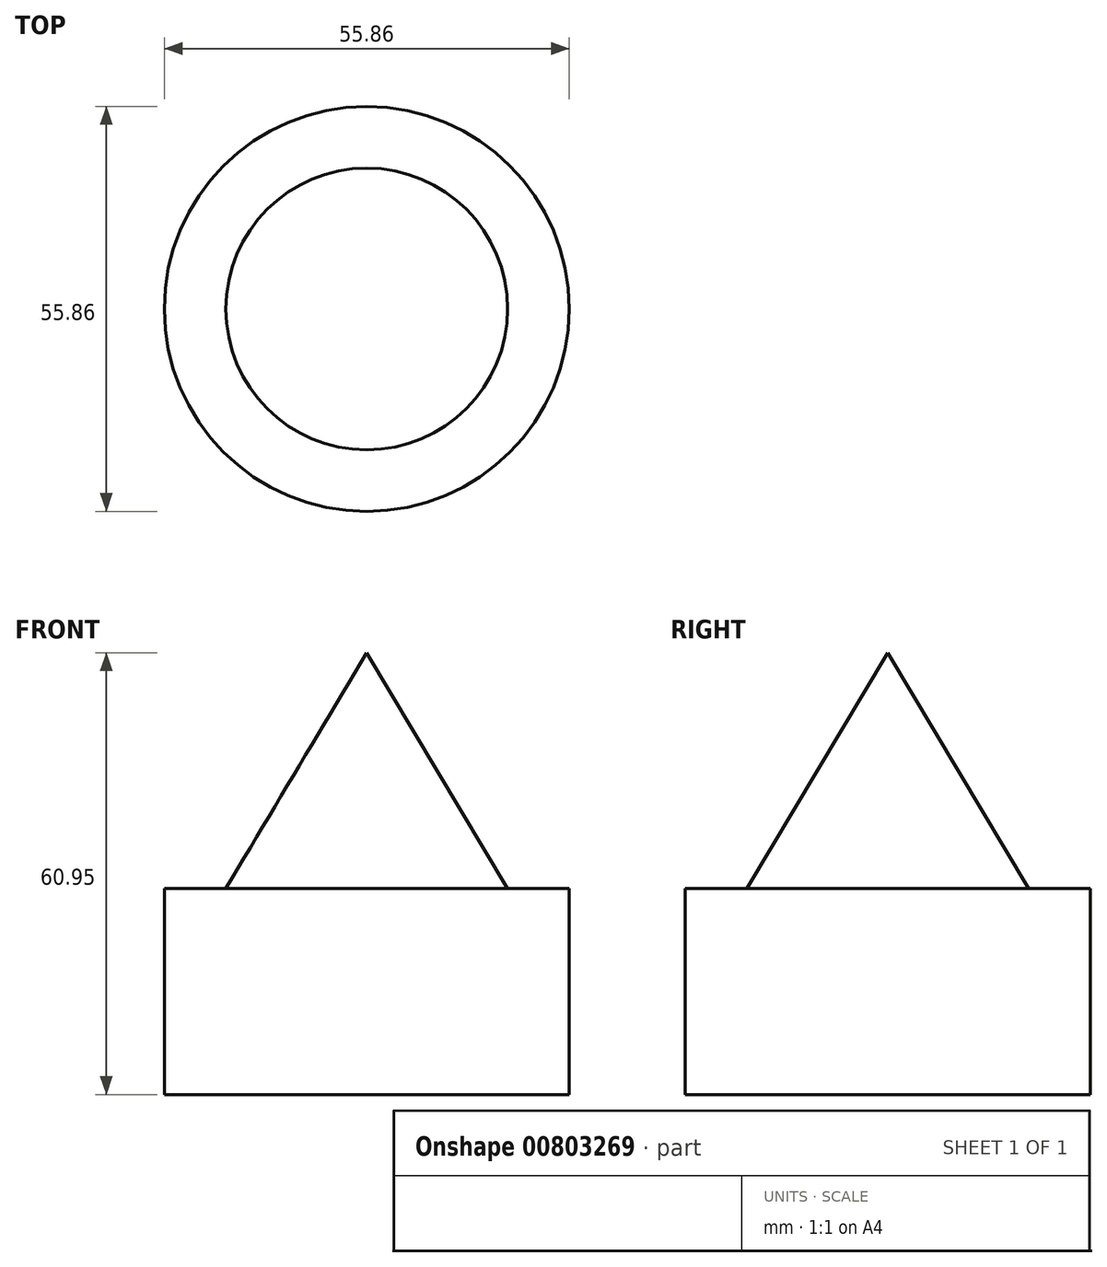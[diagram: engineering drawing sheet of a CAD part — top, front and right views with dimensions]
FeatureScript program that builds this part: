
annotation { "Feature Type Name" : "Feature", "Feature Type Description" : "" }
export const myFeature = defineFeature(function(context is Context, id is Id, definition is map)
    precondition{}
    {
        {
            var Q0;
            Q0=qCreatedBy(makeId("Front.planeOp"),FACE);
            var sketch = newSketch(context, id + "F0", { "sketchPlane" : qUnion([Q0])});
            skLineSegment(sketch, "E0", {"start": v(0, 0) * mm, "end": v(0, 46.73) * mm});
            skLineSegment(sketch, "E1", {"start": v(0, 46.73) * mm, "end": v(27.93, 0) * mm});
            skLineSegment(sketch, "E2", {"start": v(27.93, 0) * mm, "end": v(0, 0) * mm});
            skSolve(sketch);
        }
        {
            var Q0;
            Q0 = qSketchRegion(id + "F0", true);
            var Q1;
            Q1=sQuery(id+"F0.wireOp",EDGE,"E0");
            revolve(context, id + "F1", {"surfaceOperationType" : NewSurfaceOperationType.NEW, "entities" : qUnion([Q0]), "axis" : qUnion([Q1]), "revolveType" : RevolveType.FULL});
        }
        {
            var Q0;
            Q0=qCreatedBy(makeId("Right.planeOp"),FACE);
            var sketch = newSketch(context, id + "F2", { "sketchPlane" : qUnion([Q0])});
            skLineSegment(sketch, "E3", {"start": v(-15.95, 50.24) * mm, "end": v(-15.95, -22.77) * mm});
            skSolve(sketch);
        }
        {
            var Q0;
            Q0=sQuery(id+"F2.wireOp",EDGE,"E3");
            extrude(context, id + "F3", {"bodyType" : ToolBodyType.SURFACE, "surfaceEntities" : qUnion([Q0]), "endBound" : BoundingType.SYMMETRIC, "depth" : 80.26 * mm, "offsetDistance" : 25.4 * mm});
        }
        {
            var Q0;
            Q0=qCreatedBy(makeId("Right.planeOp"),FACE);
            var sketch = newSketch(context, id + "F4", { "sketchPlane" : qUnion([Q0])});
            skLineSegment(sketch, "E4", {"start": v(-36.04, 26.27) * mm, "end": v(37.52, 26.27) * mm});
            skSolve(sketch);
        }
        {
            var Q0;
            Q0 = qSketchRegion(id + "F4", true);
            var Q1;
            Q1=sQuery(id+"F4.wireOp",EDGE,"E4");
            extrude(context, id + "F5", {"entities" : qUnion([Q0]), "bodyType" : ToolBodyType.SURFACE, "surfaceEntities" : qUnion([Q1]), "endBound" : BoundingType.SYMMETRIC, "depth" : 92.96 * mm, "offsetDistance" : 25.4 * mm});
        }
        {
            var Q0;
            Q0=qCreatedBy(makeId("Front.planeOp"),FACE);
            var sketch = newSketch(context, id + "F6", { "sketchPlane" : qUnion([Q0])});
            skLineSegment(sketch, "E5", {"start": v(66.1, 39.54) * mm, "end": v(-60, 39.54) * mm});
            skSolve(sketch);
        }
        {
            var Q0;
            Q0=sQuery(id+"F6.wireOp",EDGE,"E5");
            extrude(context, id + "F7", {"bodyType" : ToolBodyType.SURFACE, "surfaceEntities" : qUnion([Q0]), "endBound" : BoundingType.SYMMETRIC, "depth" : 70.1 * mm, "offsetDistance" : 25.4 * mm});
        }
        {
            var Q0;
            Q0=qCreatedBy(makeId("Front.planeOp"),FACE);
            var sketch = newSketch(context, id + "F8", { "sketchPlane" : qUnion([Q0])});
            skLineSegment(sketch, "E6", {"start": v(-143.13, 103.57) * mm, "end": v(-239.9, 32.87) * mm});
            skSolve(sketch);
        }
        {
            var Q0;
            Q0 = qSketchRegion(id + "F8", true);
            var Q1;
            Q1=makeQuery(id+"F1.opRevolve","SWEPT_FACE",FACE,{"disambiguationData":[OSD([sQuery(id+"F0.wireOp",EDGE,"E2")])]});
            extrude(context, id + "F9", {"entities" : qUnion([Q0, Q1]), "operationType" : NewBodyOperationType.ADD, "endBound" : BoundingType.SYMMETRIC, "depth" : 28.45 * mm, "offsetDistance" : 25.4 * mm});
        }
    });
